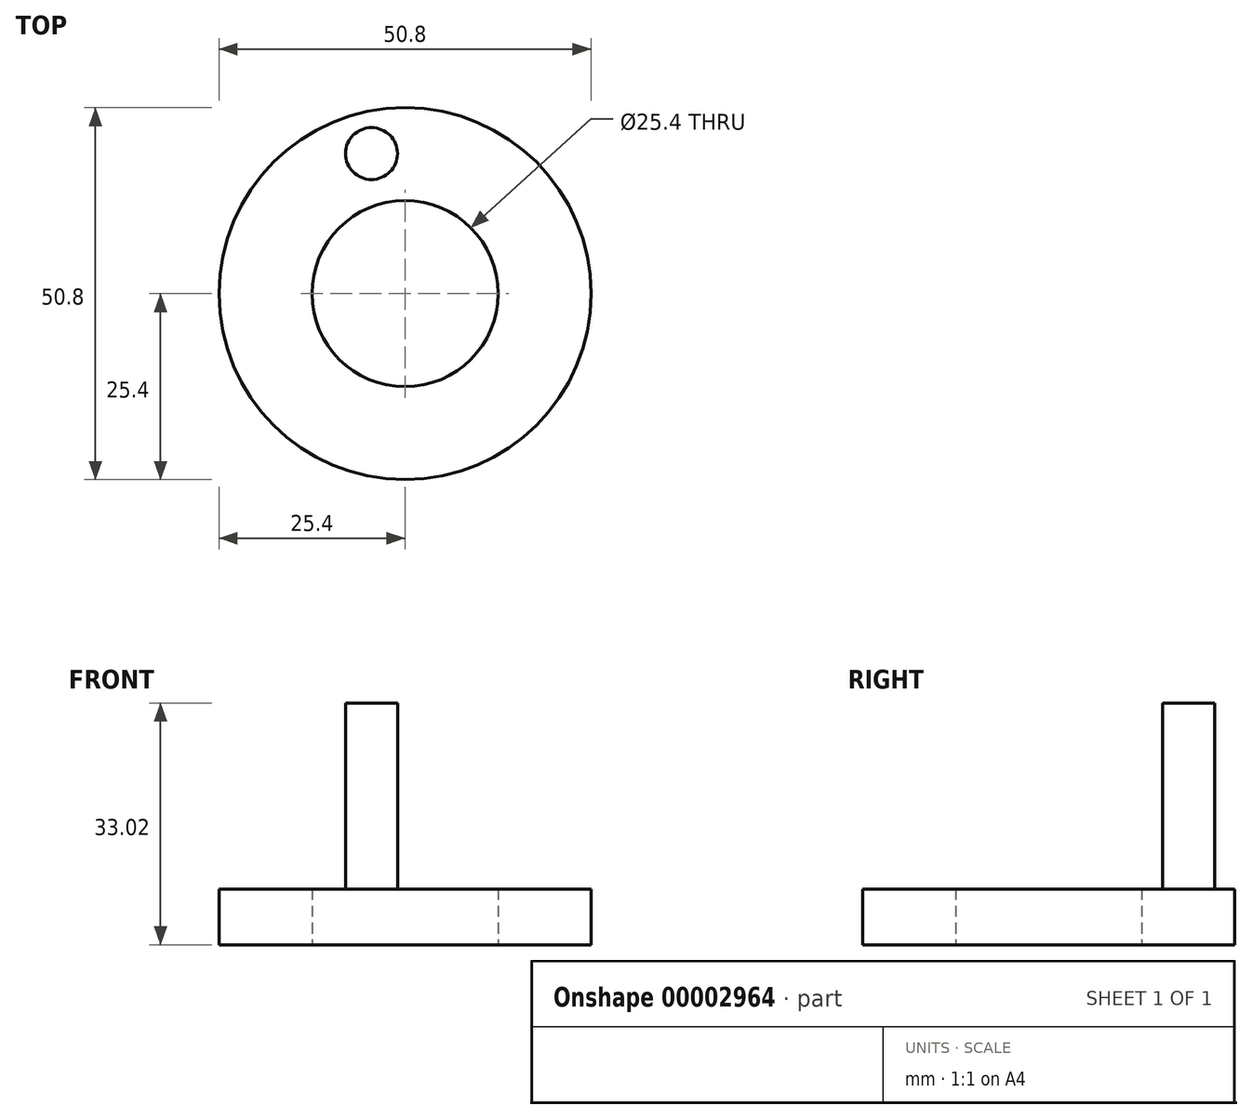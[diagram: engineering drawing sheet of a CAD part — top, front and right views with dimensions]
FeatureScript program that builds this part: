
annotation { "Feature Type Name" : "Feature", "Feature Type Description" : "" }
export const myFeature = defineFeature(function(context is Context, id is Id, definition is map)
    precondition{}
    {
        {
            var Q0;
            Q0=qCreatedBy(makeId("Top.planeOp"),FACE);
            var sketch = newSketch(context, id + "F0", { "sketchPlane" : qUnion([Q0])});
            skCircle(sketch, "E0", {"center": v(0, 0) * mm, "radius": 12.7 * mm});
            skCircle(sketch, "E1", {"center": v(0, 0) * mm, "radius": 25.4 * mm});
            skSolve(sketch);
        }
        {
            var Q0;
            Q0=makeQuery(id+"F0.imprint","IMPRINT",FACE,{"disambiguationData":[TD([[makeQuery(id+"F0.imprint","IMPRINT",EDGE,{"derivedFrom":sQuery(id+"F0.wireOp",EDGE,"E0")}),-1.0]])]});
            extrude(context, id + "F1", {"entities" : qUnion([Q0]), "depth" : 7.62 * mm});
        }
        {
            var Q0;
            Q0=makeQuery(id+"F1.opExtrude","CAP_FACE",FACE,{"disambiguationData":[OSD([sQuery(id+"F0.wireOp",EDGE,"E0"),sQuery(id+"F0.wireOp",EDGE,"E1")])],"isStart":false});
            var sketch = newSketch(context, id + "F2", { "sketchPlane" : qUnion([Q0])});
            skCircle(sketch, "E2", {"center": v(-4.58, 19.13) * mm, "radius": 3.55 * mm});
            skSolve(sketch);
        }
        {
            var Q0;
            Q0=makeQuery(id+"F2.imprint","IMPRINT",FACE,{"disambiguationData":[TD([[makeQuery(id+"F2.imprint","IMPRINT",EDGE,{"derivedFrom":sQuery(id+"F2.wireOp",EDGE,"E2")}),1.0]])]});
            extrude(context, id + "F3", {"entities" : qUnion([Q0]), "operationType" : NewBodyOperationType.ADD, "depth" : 25.4 * mm});
        }
    });
